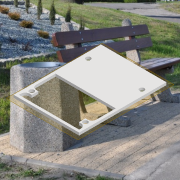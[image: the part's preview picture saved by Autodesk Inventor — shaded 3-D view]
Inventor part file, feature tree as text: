
AUTODESK INVENTOR PART (.ipt)
format: ipt  version: 2021 (Build 250183000, 183)  size: 185,344 bytes
history: native  units: mm
features: other x3, plane x1, extrude x1, sketch x1, reference x1
ambient origin geometry x8: Origin, YZ Plane, XZ Plane, XY Plane, X Axis, Y Axis, Z Axis, Center Point
bodies: Solid1 (feature_tree)
feature tree (7):
  plane  "Work Plane1"
  extrude  "Extrusion1"  Depth=3.0mm TaperAngle=0.0deg
  sketch  "Sketch1"  dims[d0=42.0mm d1=3.0mm d2=0.0mm]
  reference  "Reference1"
  other  "<userpath>\OneDrive\Pulpit\hackaton BHL\BHL 2025\Drawer.iam"
  other  "Drawer.iam"
  other  "sensorBox:1"
